# Revit family: Рондо-3
name_source: partatom
category: Осветительные приборы
units: mm (PartAtom-declared; Revit-internal decimal feet)

## family parameters
Всегда вертикально = Да
Источник света = Да
На основе рабочей плоскости = Нет
Общий = Нет
При загрузке вырезать с полостями = Нет
Размер круглого соединителя = Использовать диаметр
Тип детали = Нормальный
Точка расчета площади = Нет

## types (3) — shared parameters
ADSK_URL страницы изделия = http://www.allfresco.ru
ADSK_Артикул = ДТУ125с4
ADSK_Единица измерения = шт.
ADSK_Завод-изготовитель = ALFRESCO
ADSK_Количество фаз = 2
ADSK_Масса = 11
ADSK_Масса_Текст = 11
ADSK_Модель = Рондо-3 ДТУ-125-AF
ADSK_Напряжение = 220 В
ADSK_Полная мощность = 0 В·А
ADSK_Ток = 0 А
ADSK_Энергоэффективность = 110 лм/Вт
D_светильник = 445 мм
D_столб = 102 мм
D_фланец = 240 мм
IP Class = IP 67
d_нижний крепеж = 180 мм
d_светильник = 445 мм
d_шуруп = 378 мм
h_пластина = 5 мм
h_рассеиватель = 5 мм
h_светильник = 105 мм
r светильник = 223 мм
r_УГО = 250 мм
r_отверстия пластина = 3 мм
r_пластина = 120 мм
r_рассеиватель = 218 мм
r_столб = 51 мм
Блок аварийного питания = Нет
Видимая форма излучения при визуализации = Нет
Излучение по диаметру окружности = 445 мм
Класс защиты = 1
Класс пожароопасности = F (светильники предназначены для установки непосредственно на поверхность из нормально воспламеняемых материалов)
Климатическая зона = УХЛ1
Корпус светильника = Серый металл
Материал рассеивателя = Светотехнический ПК
Область использования = Парки, скверы, общественные пространства, городская инфраструктура
Полная установленная мощность = 0 В·А
Рассеиватель = Материал рассеивателя
Светофильтр = 16777215
Смещение цветовой температуры при затухании лампы = <Нет>
Таблица выбора = Таблица параметров светильников
Температура эксплуатации = -40 +50
Тип ИС = LED-модуль
Тип КСС = ШБ (широкая боковая)
Тип ПРА = -
Тип продукции = LED-светильник
Угол наклона = 90.00°
Цветоывая температура = 2700-5500
zero-valued in all types: ADSK_Количество фаз числовое, ADSK_Коэффициент мощности

## per-type parameters (varying)
| type | ADSK_Наименование | ADSK_Номинальная мощность | ADSK_Размер_Высота | ADSK_Фактическая мощность | h_столб | Файл фотометрической сетки |
| ДТУ125с4 Светодиодный светильник Рондо-3 ДТУ-125-AF-25Вт(d60вст) на опоре ОС 4,0м | ДТУ125с4 Светодиодный светильник Рондо-3 ДТУ-125-AF-25Вт(d60вст) на опоре ОС 4.0м | 25 Вт | 4000 мм | 25 Вт | 4190 мм | DTU-125-AF RONDO-3 25W 146x60.ies |
| ДТУ125с5 Светодиодный светильник Рондо-3 ДТУ-125-AF-50Вт(d60вст) на опоре ОС 5,0м | ДТУ125с5 Светодиодный светильник Рондо-3 ДТУ-125-AF-50Вт(d60вст) на опоре ОС 5.0м | 50 Вт | 5000 мм | 50 Вт | 5190 мм | DTU-125-AF RONDO-3 50W 146x60.ies |
| ДТУ125с6 Светодиодный светильник Рондо-3 ДТУ-125-AF-75Вт(d60вст) на опоре ОС 6,0м | ДТУ125с6 Светодиодный светильник Рондо-3 ДТУ-125-AF-75Вт(d60вст) на опоре ОС 6.0м | 75 Вт | 6000 мм | 75 Вт | 6190 мм | DTU-125-AF RONDO-3 75W 146x60.ies |

## geometry (parser evidence)
native form markers: Blend x6
no freeform markers — native parametric forms only
